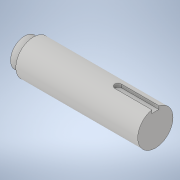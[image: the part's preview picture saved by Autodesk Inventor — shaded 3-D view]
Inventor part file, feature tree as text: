
AUTODESK INVENTOR PART (.ipt)
format: ipt  version: 2021 (Build 250183000, 183)  size: 124,928 bytes
history: native  units: in
note: dims shown in document units (in); Inventor stores cm internally (conversion verified against a paired STEP export)
features: extrude x4, sketch x4, plane x1
ambient origin geometry x8: Origin, YZ Plane, XZ Plane, XY Plane, X Axis, Y Axis, Z Axis, Center Point
bodies: Solid1 (feature_tree)
feature tree (9):
  extrude  "Extrusion1"  Depth=4.634in TaperAngle=0.0deg
  plane  "Work Plane1"
  extrude  "Extrusion9"  Depth=0.25in
  extrude  "Extrusion10"  Depth=0.125in TaperAngle=0.0deg
  extrude  "Extrusion11"  Depth=0.3125in TaperAngle=0.0deg
  sketch  "Sketch1"  dims[d0=1.25in d1=4.634in d2=0.0in]
  sketch  "Sketch9"  dims[d11=-2.0535in d26=0.25in]
  sketch  "Sketch10"  dims[d27=0.125in d28=1.313in d29=0.0in]
  sketch  "Sketch11"  dims[d30=1.0in d31=0.3125in d32=0.0in d33=1.0in d34=0.0in]
